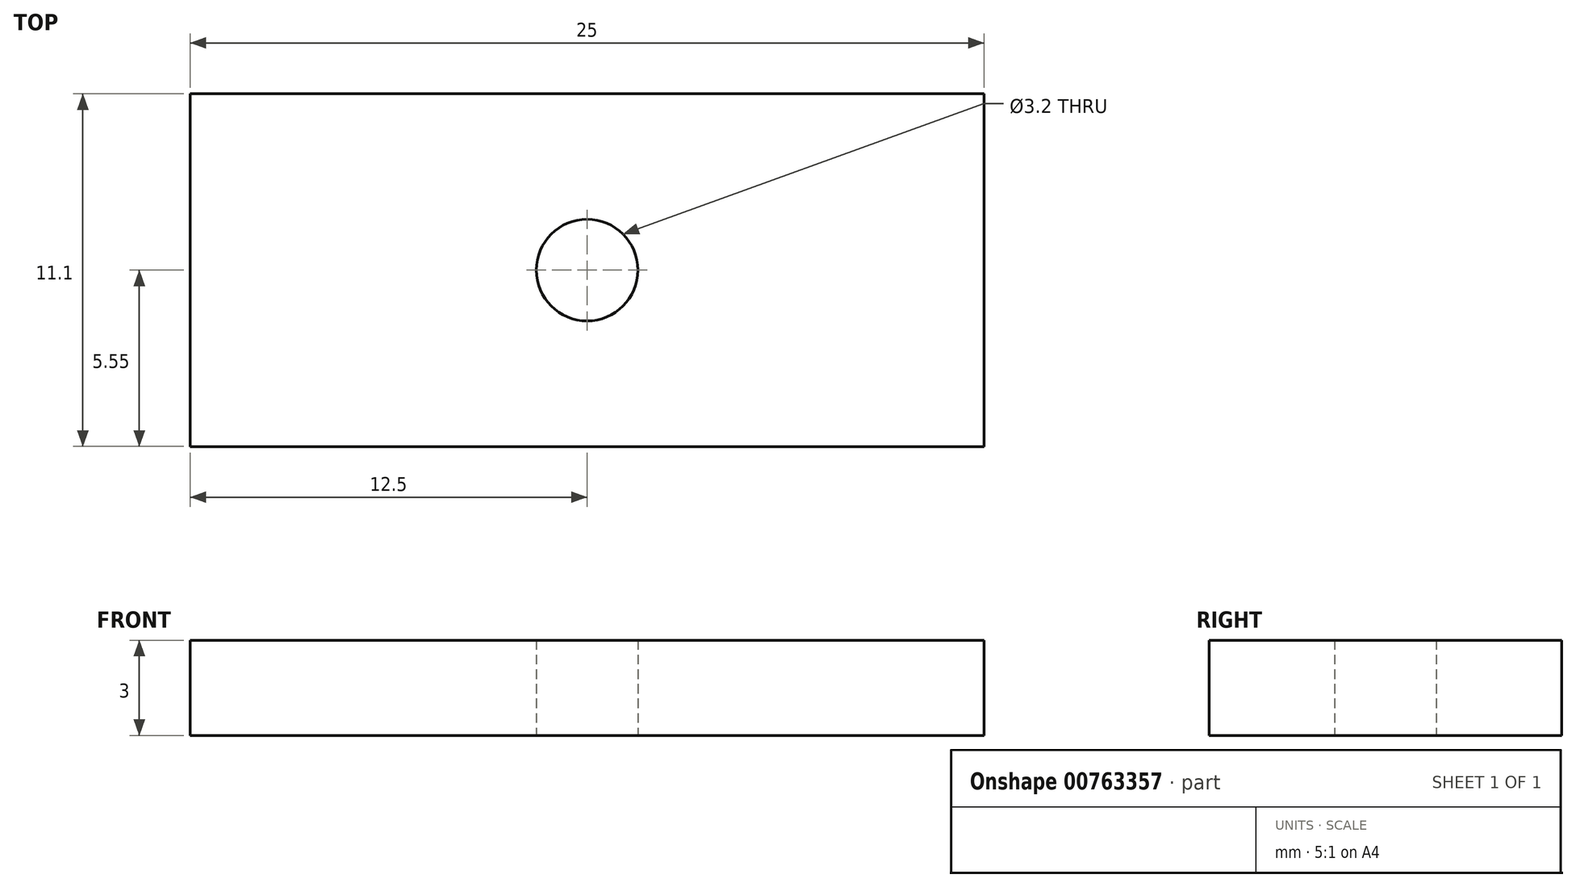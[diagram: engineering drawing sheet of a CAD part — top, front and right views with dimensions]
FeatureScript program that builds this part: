
annotation { "Feature Type Name" : "Feature", "Feature Type Description" : "" }
export const myFeature = defineFeature(function(context is Context, id is Id, definition is map)
    precondition{}
    {
        {
            var Q0;
            Q0=qCreatedBy(makeId("Top.planeOp"),FACE);
            var sketch = newSketch(context, id + "F0", { "sketchPlane" : qUnion([Q0])});
            skLineSegment(sketch, "E0.bottom", {"start": v(-12.5, 5.56) * mm, "end": v(12.5, 5.56) * mm});
            skLineSegment(sketch, "E0.top", {"start": v(-12.5, -5.56) * mm, "end": v(12.5, -5.56) * mm});
            skLineSegment(sketch, "E0.left", {"start": v(-12.5, 5.56) * mm, "end": v(-12.5, -5.56) * mm});
            skLineSegment(sketch, "E0.right", {"start": v(12.5, 5.56) * mm, "end": v(12.5, -5.56) * mm});
            skPoint(sketch, "E0.middle", {"position": v(0, 0) * mm});
            skCircle(sketch, "E1", {"center": v(0, 0) * mm, "radius": 1.6 * mm});
            skSolve(sketch);
        }
        {
            var Q0;
            Q0 = qSketchRegion(id + "F0", true);
            extrude(context, id + "F1", {"entities" : qUnion([Q0]), "depth" : 3 * mm, "offsetDistance" : 25 * mm});
        }
    });
